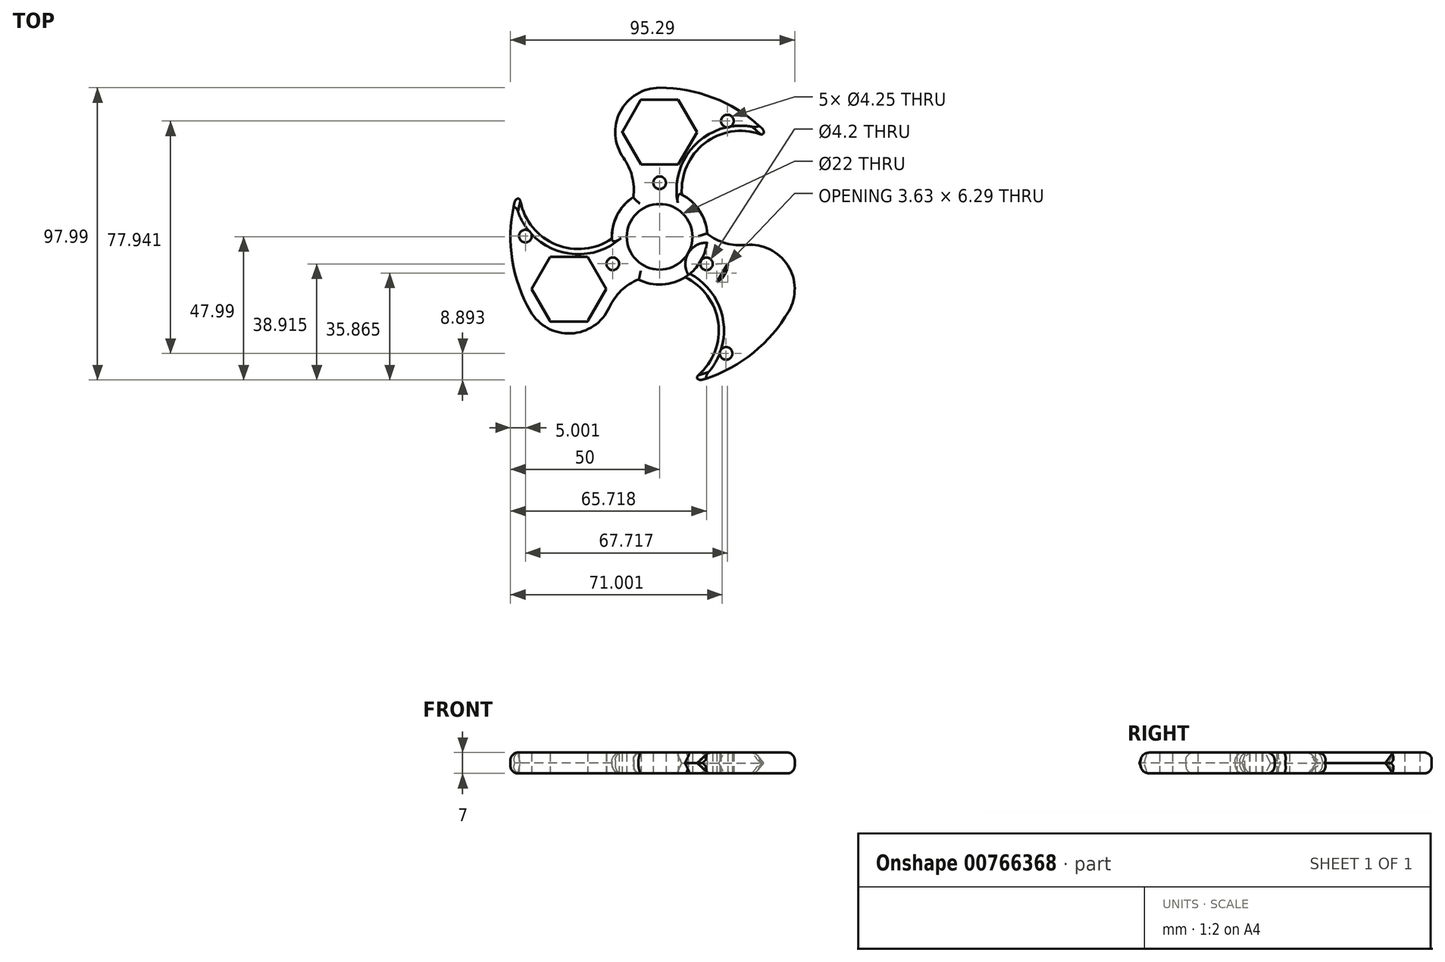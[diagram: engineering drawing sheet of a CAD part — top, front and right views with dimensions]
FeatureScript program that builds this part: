
annotation { "Feature Type Name" : "Feature", "Feature Type Description" : "" }
export const myFeature = defineFeature(function(context is Context, id is Id, definition is map)
    precondition{}
    {
        {
            var Q0;
            Q0=qCreatedBy(makeId("Top.planeOp"),FACE);
            var sketch = newSketch(context, id + "F0", { "sketchPlane" : qUnion([Q0])});
            skCircle(sketch, "E0", {"center": v(0, 0) * mm, "radius": 11 * mm});
            skArc(sketch, "E1", {"start": v(-43.3, 25) * mm, "mid": v(-50, 0) * mm, "end": v(-43.3, -25) * mm});
            skLineSegment(sketch, "E2", {"start": v(0, 50) * mm, "end": v(0, 0) * mm});
            skLineSegment(sketch, "E3", {"start": v(0, 0) * mm, "end": v(-43.3, -25) * mm});
            skLineSegment(sketch, "E4", {"start": v(-43.3, -25) * mm, "end": v(0, 0) * mm});
            skLineSegment(sketch, "E5", {"start": v(0, 0) * mm, "end": v(43.3, -25) * mm});
            skCircle(sketch, "E6.cCircle", {"center": v(0, 35.12) * mm, "radius": 10.88 * mm, "construction": true});
            skLineSegment(sketch, "E6.0", {"start": v(12.56, 35.12) * mm, "end": v(6.28, 24.25) * mm});
            skLineSegment(sketch, "E6.1", {"start": v(6.28, 24.25) * mm, "end": v(-6.28, 24.25) * mm});
            skLineSegment(sketch, "E6.2", {"start": v(-6.28, 24.25) * mm, "end": v(-12.56, 35.13) * mm});
            skLineSegment(sketch, "E6.3", {"start": v(-12.56, 35.13) * mm, "end": v(-6.28, 46) * mm});
            skLineSegment(sketch, "E6.4", {"start": v(-6.28, 46) * mm, "end": v(6.28, 46) * mm});
            skLineSegment(sketch, "E6.5", {"start": v(6.28, 46) * mm, "end": v(12.56, 35.12) * mm});
            skPoint(sketch, "E6.0.midPoint", {"position": v(9.42, 29.69) * mm});
            skCircle(sketch, "E7.cCircle", {"center": v(30.42, -17.56) * mm, "radius": 10.88 * mm, "construction": true});
            skLineSegment(sketch, "E7.0", {"start": v(36.7, -6.69) * mm, "end": v(42.98, -17.56) * mm});
            skLineSegment(sketch, "E7.1", {"start": v(42.98, -17.56) * mm, "end": v(36.7, -28.44) * mm});
            skLineSegment(sketch, "E7.2", {"start": v(36.7, -28.44) * mm, "end": v(24.14, -28.44) * mm});
            skLineSegment(sketch, "E7.3", {"start": v(24.14, -28.44) * mm, "end": v(17.86, -17.56) * mm});
            skLineSegment(sketch, "E7.4", {"start": v(17.86, -17.56) * mm, "end": v(24.14, -6.69) * mm});
            skLineSegment(sketch, "E7.5", {"start": v(24.14, -6.69) * mm, "end": v(36.7, -6.69) * mm});
            skPoint(sketch, "E7.0.midPoint", {"position": v(39.84, -12.12) * mm});
            skCircle(sketch, "E8.cCircle", {"center": v(-30.42, -17.56) * mm, "radius": 10.88 * mm, "construction": true});
            skLineSegment(sketch, "E8.0", {"start": v(-17.86, -17.56) * mm, "end": v(-24.14, -28.44) * mm});
            skLineSegment(sketch, "E8.1", {"start": v(-24.14, -28.44) * mm, "end": v(-36.7, -28.44) * mm});
            skLineSegment(sketch, "E8.2", {"start": v(-36.7, -28.44) * mm, "end": v(-42.98, -17.56) * mm});
            skLineSegment(sketch, "E8.3", {"start": v(-42.98, -17.56) * mm, "end": v(-36.7, -6.69) * mm});
            skLineSegment(sketch, "E8.4", {"start": v(-36.7, -6.69) * mm, "end": v(-24.14, -6.69) * mm});
            skLineSegment(sketch, "E8.5", {"start": v(-24.14, -6.69) * mm, "end": v(-17.86, -17.56) * mm});
            skPoint(sketch, "E8.0.midPoint", {"position": v(-21, -23) * mm});
            skCircle(sketch, "E9", {"center": v(0, 35.12) * mm, "radius": 14.88 * mm});
            skCircle(sketch, "E10", {"center": v(30.42, -17.56) * mm, "radius": 14.88 * mm});
            skCircle(sketch, "E11", {"center": v(-30.42, -17.56) * mm, "radius": 14.87 * mm});
            skCircle(sketch, "E12", {"center": v(0, 0) * mm, "radius": 16 * mm});
            skCircle(sketch, "E13", {"center": v(0, 18.13) * mm, "radius": 2.13 * mm});
            skCircle(sketch, "E14", {"center": v(0, 18.13) * mm, "radius": 7.13 * mm});
            skCircle(sketch, "E15", {"center": v(15.72, -9.07) * mm, "radius": 2.1 * mm});
            skCircle(sketch, "E16", {"center": v(15.72, -9.07) * mm, "radius": 7.1 * mm});
            skCircle(sketch, "E17", {"center": v(-15.7, -9.06) * mm, "radius": 2.13 * mm});
            skCircle(sketch, "E18", {"center": v(-15.7, -9.06) * mm, "radius": 7.13 * mm});
            skLineSegment(sketch, "E19", {"start": v(0, 0) * mm, "end": v(-13.86, 8) * mm});
            skLineSegment(sketch, "E20", {"start": v(0, 0) * mm, "end": v(13.86, 8) * mm});
            skLineSegment(sketch, "E21", {"start": v(0, 0) * mm, "end": v(0, -16) * mm});
            skArc(sketch, "E22", {"start": v(-43.3, 25) * mm, "mid": v(-26.34, -2.82) * mm, "end": v(-12.11, 26.5) * mm});
            skArc(sketch, "E23", {"start": v(43.3, 25) * mm, "mid": v(10.73, 24.22) * mm, "end": v(29, -2.76) * mm});
            skArc(sketch, "E24", {"start": v(0, -50) * mm, "mid": v(15.61, -21.4) * mm, "end": v(-16.89, -23.74) * mm});
            skArc(sketch, "E25.trimOffspring", {"start": v(0, -50) * mm, "mid": v(25, -43.3) * mm, "end": v(43.3, -25) * mm});
            skArc(sketch, "E26.trimOffspring", {"start": v(43.3, 25) * mm, "mid": v(25, 43.3) * mm, "end": v(0, 50) * mm});
            skPoint(sketch, "E27", {"position": v(22.72, 38.84) * mm});
            skPoint(sketch, "E28", {"position": v(22.28, -39.1) * mm});
            skPoint(sketch, "E29", {"position": v(-45, 0.25) * mm});
            skSolve(sketch);
        }
        {
            var Q0;
            {var subQ1=sQuery(id+"F0.wireOp",EDGE,"E6.2");Q0=makeQuery(id+"F0.imprint","IMPRINT",FACE,{"disambiguationData":[TD([[makeQuery(id+"F0.imprint","IMPRINT",EDGE,{"derivedFrom":subQ1}),1.0]])]});}
            var Q1;
            {var subQ5=sQuery(id+"F0.wireOp",EDGE,"E6.0");Q1=makeQuery(id+"F0.imprint","IMPRINT",FACE,{"disambiguationData":[TD([[makeQuery(id+"F0.imprint","IMPRINT",EDGE,{"derivedFrom":subQ5}),1.0]])]});}
            var Q2;
            {var subQ0=sQuery(id+"F0.wireOp",EDGE,"E6.1");var subQ1=sQuery(id+"F0.wireOp",EDGE,"E2");var subQ2=makeQuery(id+"F0.imprint","INTERSECT",VERTEX,{"derivedFrom":[subQ1,subQ0]});Q2=makeQuery(id+"F0.imprint","IMPRINT",FACE,{"disambiguationData":[TD([[makeQuery(id+"F0.imprint","IMPRINT",EDGE,{"disambiguationData":[TD([[subQ2,1.0]])],"derivedFrom":subQ0}),1.0]])]});}
            var Q3;
            {var subQ0=sQuery(id+"F0.wireOp",EDGE,"E6.1");var subQ1=sQuery(id+"F0.wireOp",EDGE,"E2");var subQ2=makeQuery(id+"F0.imprint","INTERSECT",VERTEX,{"derivedFrom":[subQ1,subQ0]});Q3=makeQuery(id+"F0.imprint","IMPRINT",FACE,{"disambiguationData":[TD([[makeQuery(id+"F0.imprint","IMPRINT",EDGE,{"disambiguationData":[TD([[subQ2,-1.0]])],"derivedFrom":subQ0}),1.0]])]});}
            var Q4;
            {var subQ0=sQuery(id+"F0.wireOp",EDGE,"E22");var subQ1=sQuery(id+"F0.wireOp",EDGE,"E9");var subQ2=makeQuery(id+"F0.imprint","INTERSECT",VERTEX,{"derivedFrom":[subQ1,subQ0]});Q4=makeQuery(id+"F0.imprint","IMPRINT",FACE,{"disambiguationData":[TD([[makeQuery(id+"F0.imprint","IMPRINT",EDGE,{"disambiguationData":[TD([[subQ2,-1.0]])],"derivedFrom":subQ1}),-1.0]])]});}
            var Q5;
            {var subQ0=sQuery(id+"F0.wireOp",EDGE,"E23");var subQ1=sQuery(id+"F0.wireOp",EDGE,"E9");var subQ2=makeQuery(id+"F0.imprint","INTERSECT",VERTEX,{"derivedFrom":[subQ1,subQ0]});Q5=makeQuery(id+"F0.imprint","IMPRINT",FACE,{"disambiguationData":[TD([[makeQuery(id+"F0.imprint","IMPRINT",EDGE,{"disambiguationData":[TD([[subQ2,1.0]])],"derivedFrom":subQ1}),-1.0]])]});}
            var Q6;
            {var subQ3=sQuery(id+"F0.wireOp",EDGE,"E22");var subQ5=sQuery(id+"F0.wireOp",EDGE,"E12");var subQ6=makeQuery(id+"F0.imprint","INTERSECT",VERTEX,{"disambiguationData":[OD(0.0)],"derivedFrom":[subQ5,subQ3]});Q6=makeQuery(id+"F0.imprint","IMPRINT",FACE,{"disambiguationData":[TD([[makeQuery(id+"F0.imprint","IMPRINT",EDGE,{"disambiguationData":[TD([[subQ6,1.0]])],"derivedFrom":subQ5}),1.0]])]});}
            var Q7;
            {var subQ1=sQuery(id+"F0.wireOp",EDGE,"E12");var subQ7=sQuery(id+"F0.wireOp",EDGE,"E23");var subQ9=makeQuery(id+"F0.imprint","INTERSECT",VERTEX,{"disambiguationData":[OD(1.0)],"derivedFrom":[subQ1,subQ7]});Q7=makeQuery(id+"F0.imprint","IMPRINT",FACE,{"disambiguationData":[TD([[makeQuery(id+"F0.imprint","IMPRINT",EDGE,{"disambiguationData":[TD([[subQ9,-1.0]])],"derivedFrom":subQ1}),1.0]])]});}
            var Q8;
            {var subQ1=sQuery(id+"F0.wireOp",EDGE,"E12");var subQ5=sQuery(id+"F0.wireOp",EDGE,"E22");var subQ6=makeQuery(id+"F0.imprint","INTERSECT",VERTEX,{"disambiguationData":[OD(1.0)],"derivedFrom":[subQ1,subQ5]});Q8=makeQuery(id+"F0.imprint","IMPRINT",FACE,{"disambiguationData":[TD([[makeQuery(id+"F0.imprint","IMPRINT",EDGE,{"disambiguationData":[TD([[subQ6,-1.0]])],"derivedFrom":subQ1}),1.0]])]});}
            var Q9;
            {var subQ1=sQuery(id+"F0.wireOp",EDGE,"E12");var subQ5=sQuery(id+"F0.wireOp",EDGE,"E24");var subQ6=makeQuery(id+"F0.imprint","INTERSECT",VERTEX,{"disambiguationData":[OD(0.0)],"derivedFrom":[subQ1,subQ5]});Q9=makeQuery(id+"F0.imprint","IMPRINT",FACE,{"disambiguationData":[TD([[makeQuery(id+"F0.imprint","IMPRINT",EDGE,{"disambiguationData":[TD([[subQ6,1.0]])],"derivedFrom":subQ1}),1.0]])]});}
            var Q10;
            {var subQ5=sQuery(id+"F0.wireOp",EDGE,"E21");var subQ6=sQuery(id+"F0.wireOp",EDGE,"E0");var subQ7=makeQuery(id+"F0.imprint","INTERSECT",VERTEX,{"derivedFrom":[subQ6,subQ5]});Q10=makeQuery(id+"F0.imprint","IMPRINT",FACE,{"disambiguationData":[TD([[makeQuery(id+"F0.imprint","IMPRINT",EDGE,{"disambiguationData":[TD([[subQ7,-1.0]])],"derivedFrom":subQ6}),-1.0]])]});}
            var Q11;
            {var subQ1=sQuery(id+"F0.wireOp",EDGE,"E0");var subQ9=sQuery(id+"F0.wireOp",EDGE,"E20");var subQ11=makeQuery(id+"F0.imprint","INTERSECT",VERTEX,{"derivedFrom":[subQ1,subQ9]});Q11=makeQuery(id+"F0.imprint","IMPRINT",FACE,{"disambiguationData":[TD([[makeQuery(id+"F0.imprint","IMPRINT",EDGE,{"disambiguationData":[TD([[subQ11,1.0]])],"derivedFrom":subQ1}),-1.0]])]});}
            var Q12;
            {var subQ0=sQuery(id+"F0.wireOp",EDGE,"E23");var subQ1=sQuery(id+"F0.wireOp",EDGE,"E10");var subQ2=makeQuery(id+"F0.imprint","INTERSECT",VERTEX,{"derivedFrom":[subQ1,subQ0]});Q12=makeQuery(id+"F0.imprint","IMPRINT",FACE,{"disambiguationData":[TD([[makeQuery(id+"F0.imprint","IMPRINT",EDGE,{"disambiguationData":[TD([[subQ2,-1.0]])],"derivedFrom":subQ1}),-1.0]])]});}
            var Q13;
            {var subQ0=sQuery(id+"F0.wireOp",EDGE,"E24");var subQ1=sQuery(id+"F0.wireOp",EDGE,"E10");var subQ2=makeQuery(id+"F0.imprint","INTERSECT",VERTEX,{"derivedFrom":[subQ1,subQ0]});Q13=makeQuery(id+"F0.imprint","IMPRINT",FACE,{"disambiguationData":[TD([[makeQuery(id+"F0.imprint","IMPRINT",EDGE,{"disambiguationData":[TD([[subQ2,1.0]])],"derivedFrom":subQ1}),-1.0]])]});}
            var Q14;
            {var subQ0=sQuery(id+"F0.wireOp",EDGE,"E7.2");Q14=makeQuery(id+"F0.imprint","IMPRINT",FACE,{"disambiguationData":[TD([[makeQuery(id+"F0.imprint","IMPRINT",EDGE,{"derivedFrom":subQ0}),1.0]])]});}
            var Q15;
            {var subQ5=sQuery(id+"F0.wireOp",EDGE,"E7.0");Q15=makeQuery(id+"F0.imprint","IMPRINT",FACE,{"disambiguationData":[TD([[makeQuery(id+"F0.imprint","IMPRINT",EDGE,{"derivedFrom":subQ5}),1.0]])]});}
            var Q16;
            {var subQ0=sQuery(id+"F0.wireOp",EDGE,"E25.trimOffspring");Q16=makeQuery(id+"F0.imprint","IMPRINT",FACE,{"disambiguationData":[TD([[makeQuery(id+"F0.imprint","IMPRINT",EDGE,{"derivedFrom":subQ0}),1.0]])]});}
            var Q17;
            {var subQ0=sQuery(id+"F0.wireOp",EDGE,"E7.4");var subQ1=sQuery(id+"F0.wireOp",EDGE,"E5");var subQ2=makeQuery(id+"F0.imprint","INTERSECT",VERTEX,{"derivedFrom":[subQ1,subQ0]});Q17=makeQuery(id+"F0.imprint","IMPRINT",FACE,{"disambiguationData":[TD([[makeQuery(id+"F0.imprint","IMPRINT",EDGE,{"disambiguationData":[TD([[subQ2,1.0]])],"derivedFrom":subQ0}),1.0]])]});}
            var Q18;
            {var subQ0=sQuery(id+"F0.wireOp",EDGE,"E7.4");var subQ1=sQuery(id+"F0.wireOp",EDGE,"E5");var subQ2=makeQuery(id+"F0.imprint","INTERSECT",VERTEX,{"derivedFrom":[subQ1,subQ0]});Q18=makeQuery(id+"F0.imprint","IMPRINT",FACE,{"disambiguationData":[TD([[makeQuery(id+"F0.imprint","IMPRINT",EDGE,{"disambiguationData":[TD([[subQ2,-1.0]])],"derivedFrom":subQ0}),1.0]])]});}
            var Q19;
            {var subQ0=sQuery(id+"F0.wireOp",EDGE,"E26.trimOffspring");Q19=makeQuery(id+"F0.imprint","IMPRINT",FACE,{"disambiguationData":[TD([[makeQuery(id+"F0.imprint","IMPRINT",EDGE,{"derivedFrom":subQ0}),1.0]])]});}
            var Q20;
            {var subQ0=sQuery(id+"F0.wireOp",EDGE,"E14");var subQ1=sQuery(id+"F0.wireOp",EDGE,"E9");var subQ2=makeQuery(id+"F0.imprint","INTERSECT",VERTEX,{"disambiguationData":[OD(0.0)],"derivedFrom":[subQ1,subQ0]});Q20=makeQuery(id+"F0.imprint","IMPRINT",FACE,{"disambiguationData":[TD([[makeQuery(id+"F0.imprint","IMPRINT",EDGE,{"disambiguationData":[TD([[subQ2,-1.0]])],"derivedFrom":subQ0}),1.0]])]});}
            var Q21;
            {var subQ0=sQuery(id+"F0.wireOp",EDGE,"E14");var subQ1=sQuery(id+"F0.wireOp",EDGE,"E9");var subQ2=makeQuery(id+"F0.imprint","INTERSECT",VERTEX,{"disambiguationData":[OD(1.0)],"derivedFrom":[subQ1,subQ0]});Q21=makeQuery(id+"F0.imprint","IMPRINT",FACE,{"disambiguationData":[TD([[makeQuery(id+"F0.imprint","IMPRINT",EDGE,{"disambiguationData":[TD([[subQ2,1.0]])],"derivedFrom":subQ0}),1.0]])]});}
            var Q22;
            {var subQ0=sQuery(id+"F0.wireOp",EDGE,"E14");var subQ3=sQuery(id+"F0.wireOp",EDGE,"E12");var subQ5=makeQuery(id+"F0.imprint","INTERSECT",VERTEX,{"disambiguationData":[OD(0.0)],"derivedFrom":[subQ3,subQ0]});Q22=makeQuery(id+"F0.imprint","IMPRINT",FACE,{"disambiguationData":[TD([[makeQuery(id+"F0.imprint","IMPRINT",EDGE,{"disambiguationData":[TD([[subQ5,-1.0]])],"derivedFrom":subQ3}),1.0]])]});}
            var Q23;
            {var subQ0=sQuery(id+"F0.wireOp",EDGE,"E14");var subQ3=sQuery(id+"F0.wireOp",EDGE,"E12");var subQ5=makeQuery(id+"F0.imprint","INTERSECT",VERTEX,{"disambiguationData":[OD(1.0)],"derivedFrom":[subQ3,subQ0]});Q23=makeQuery(id+"F0.imprint","IMPRINT",FACE,{"disambiguationData":[TD([[makeQuery(id+"F0.imprint","IMPRINT",EDGE,{"disambiguationData":[TD([[subQ5,1.0]])],"derivedFrom":subQ3}),1.0]])]});}
            var Q24;
            {var subQ0=sQuery(id+"F0.wireOp",EDGE,"E16");var subQ1=sQuery(id+"F0.wireOp",EDGE,"E5");var subQ2=makeQuery(id+"F0.imprint","INTERSECT",VERTEX,{"disambiguationData":[OD(0.0)],"derivedFrom":[subQ1,subQ0]});Q24=makeQuery(id+"F0.imprint","IMPRINT",FACE,{"disambiguationData":[TD([[makeQuery(id+"F0.imprint","IMPRINT",EDGE,{"disambiguationData":[TD([[subQ2,-1.0]])],"derivedFrom":subQ1}),1.0]])]});}
            var Q25;
            {var subQ0=sQuery(id+"F0.wireOp",EDGE,"E16");var subQ1=sQuery(id+"F0.wireOp",EDGE,"E5");var subQ2=makeQuery(id+"F0.imprint","INTERSECT",VERTEX,{"disambiguationData":[OD(0.0)],"derivedFrom":[subQ1,subQ0]});Q25=makeQuery(id+"F0.imprint","IMPRINT",FACE,{"disambiguationData":[TD([[makeQuery(id+"F0.imprint","IMPRINT",EDGE,{"disambiguationData":[TD([[subQ2,-1.0]])],"derivedFrom":subQ1}),-1.0]])]});}
            var Q26;
            {var subQ1=sQuery(id+"F0.wireOp",EDGE,"E5");var subQ5=sQuery(id+"F0.wireOp",EDGE,"E12");var subQ6=makeQuery(id+"F0.imprint","INTERSECT",VERTEX,{"derivedFrom":[subQ1,subQ5]});Q26=makeQuery(id+"F0.imprint","IMPRINT",FACE,{"disambiguationData":[TD([[makeQuery(id+"F0.imprint","IMPRINT",EDGE,{"disambiguationData":[TD([[subQ6,-1.0]])],"derivedFrom":subQ1}),-1.0]])]});}
            var Q27;
            {var subQ1=sQuery(id+"F0.wireOp",EDGE,"E5");var subQ7=sQuery(id+"F0.wireOp",EDGE,"E12");var subQ8=makeQuery(id+"F0.imprint","INTERSECT",VERTEX,{"derivedFrom":[subQ1,subQ7]});Q27=makeQuery(id+"F0.imprint","IMPRINT",FACE,{"disambiguationData":[TD([[makeQuery(id+"F0.imprint","IMPRINT",EDGE,{"disambiguationData":[TD([[subQ8,-1.0]])],"derivedFrom":subQ1}),1.0]])]});}
            var Q28;
            {var subQ0=sQuery(id+"F0.wireOp",EDGE,"E1");Q28=makeQuery(id+"F0.imprint","IMPRINT",FACE,{"disambiguationData":[TD([[makeQuery(id+"F0.imprint","IMPRINT",EDGE,{"derivedFrom":subQ0}),1.0]])]});}
            var Q29;
            {var subQ1=sQuery(id+"F0.wireOp",EDGE,"E8.3");Q29=makeQuery(id+"F0.imprint","IMPRINT",FACE,{"disambiguationData":[TD([[makeQuery(id+"F0.imprint","IMPRINT",EDGE,{"derivedFrom":subQ1}),1.0]])]});}
            var Q30;
            {var subQ4=sQuery(id+"F0.wireOp",EDGE,"E8.0");Q30=makeQuery(id+"F0.imprint","IMPRINT",FACE,{"disambiguationData":[TD([[makeQuery(id+"F0.imprint","IMPRINT",EDGE,{"derivedFrom":subQ4}),1.0]])]});}
            var Q31;
            {var subQ0=sQuery(id+"F0.wireOp",EDGE,"E24");var subQ1=sQuery(id+"F0.wireOp",EDGE,"E11");var subQ2=makeQuery(id+"F0.imprint","INTERSECT",VERTEX,{"derivedFrom":[subQ1,subQ0]});Q31=makeQuery(id+"F0.imprint","IMPRINT",FACE,{"disambiguationData":[TD([[makeQuery(id+"F0.imprint","IMPRINT",EDGE,{"disambiguationData":[TD([[subQ2,-1.0]])],"derivedFrom":subQ1}),-1.0]])]});}
            var Q32;
            {var subQ0=sQuery(id+"F0.wireOp",EDGE,"E22");var subQ1=sQuery(id+"F0.wireOp",EDGE,"E11");var subQ2=makeQuery(id+"F0.imprint","INTERSECT",VERTEX,{"derivedFrom":[subQ1,subQ0]});Q32=makeQuery(id+"F0.imprint","IMPRINT",FACE,{"disambiguationData":[TD([[makeQuery(id+"F0.imprint","IMPRINT",EDGE,{"disambiguationData":[TD([[subQ2,1.0]])],"derivedFrom":subQ1}),-1.0]])]});}
            var Q33;
            {var subQ0=sQuery(id+"F0.wireOp",EDGE,"E8.5");var subQ1=sQuery(id+"F0.wireOp",EDGE,"E4");var subQ2=makeQuery(id+"F0.imprint","INTERSECT",VERTEX,{"derivedFrom":[subQ1,subQ0]});Q33=makeQuery(id+"F0.imprint","IMPRINT",FACE,{"disambiguationData":[TD([[makeQuery(id+"F0.imprint","IMPRINT",EDGE,{"disambiguationData":[TD([[subQ2,-1.0]])],"derivedFrom":subQ0}),1.0]])]});}
            var Q34;
            {var subQ0=sQuery(id+"F0.wireOp",EDGE,"E8.5");var subQ1=sQuery(id+"F0.wireOp",EDGE,"E4");var subQ2=makeQuery(id+"F0.imprint","INTERSECT",VERTEX,{"derivedFrom":[subQ1,subQ0]});Q34=makeQuery(id+"F0.imprint","IMPRINT",FACE,{"disambiguationData":[TD([[makeQuery(id+"F0.imprint","IMPRINT",EDGE,{"disambiguationData":[TD([[subQ2,1.0]])],"derivedFrom":subQ0}),1.0]])]});}
            var Q35;
            {var subQ0=sQuery(id+"F0.wireOp",EDGE,"E18");var subQ1=sQuery(id+"F0.wireOp",EDGE,"E11");var subQ2=makeQuery(id+"F0.imprint","INTERSECT",VERTEX,{"disambiguationData":[OD(1.0)],"derivedFrom":[subQ1,subQ0]});Q35=makeQuery(id+"F0.imprint","IMPRINT",FACE,{"disambiguationData":[TD([[makeQuery(id+"F0.imprint","IMPRINT",EDGE,{"disambiguationData":[TD([[subQ2,1.0]])],"derivedFrom":subQ0}),1.0]])]});}
            var Q36;
            {var subQ0=sQuery(id+"F0.wireOp",EDGE,"E18");var subQ1=sQuery(id+"F0.wireOp",EDGE,"E11");var subQ2=makeQuery(id+"F0.imprint","INTERSECT",VERTEX,{"disambiguationData":[OD(0.0)],"derivedFrom":[subQ1,subQ0]});Q36=makeQuery(id+"F0.imprint","IMPRINT",FACE,{"disambiguationData":[TD([[makeQuery(id+"F0.imprint","IMPRINT",EDGE,{"disambiguationData":[TD([[subQ2,-1.0]])],"derivedFrom":subQ0}),1.0]])]});}
            var Q37;
            {var subQ0=sQuery(id+"F0.wireOp",EDGE,"E18");var subQ3=sQuery(id+"F0.wireOp",EDGE,"E12");var subQ5=makeQuery(id+"F0.imprint","INTERSECT",VERTEX,{"disambiguationData":[OD(1.0)],"derivedFrom":[subQ3,subQ0]});Q37=makeQuery(id+"F0.imprint","IMPRINT",FACE,{"disambiguationData":[TD([[makeQuery(id+"F0.imprint","IMPRINT",EDGE,{"disambiguationData":[TD([[subQ5,1.0]])],"derivedFrom":subQ3}),1.0]])]});}
            var Q38;
            {var subQ0=sQuery(id+"F0.wireOp",EDGE,"E18");var subQ3=sQuery(id+"F0.wireOp",EDGE,"E12");var subQ5=makeQuery(id+"F0.imprint","INTERSECT",VERTEX,{"disambiguationData":[OD(0.0)],"derivedFrom":[subQ3,subQ0]});Q38=makeQuery(id+"F0.imprint","IMPRINT",FACE,{"disambiguationData":[TD([[makeQuery(id+"F0.imprint","IMPRINT",EDGE,{"disambiguationData":[TD([[subQ5,-1.0]])],"derivedFrom":subQ3}),1.0]])]});}
            var Q39;
            {var subQ0=sQuery(id+"F0.wireOp",EDGE,"E19");var subQ1=sQuery(id+"F0.wireOp",EDGE,"E12");var subQ2=makeQuery(id+"F0.imprint","INTERSECT",VERTEX,{"derivedFrom":[subQ1,subQ0]});Q39=makeQuery(id+"F0.imprint","IMPRINT",FACE,{"disambiguationData":[TD([[makeQuery(id+"F0.imprint","IMPRINT",EDGE,{"disambiguationData":[TD([[subQ2,-1.0]])],"derivedFrom":subQ1}),1.0]])]});}
            var Q40;
            {var subQ0=sQuery(id+"F0.wireOp",EDGE,"E19");var subQ1=sQuery(id+"F0.wireOp",EDGE,"E12");var subQ2=makeQuery(id+"F0.imprint","INTERSECT",VERTEX,{"derivedFrom":[subQ1,subQ0]});Q40=makeQuery(id+"F0.imprint","IMPRINT",FACE,{"disambiguationData":[TD([[makeQuery(id+"F0.imprint","IMPRINT",EDGE,{"disambiguationData":[TD([[subQ2,1.0]])],"derivedFrom":subQ1}),1.0]])]});}
            var Q41;
            {var subQ0=sQuery(id+"F0.wireOp",EDGE,"E20");var subQ1=sQuery(id+"F0.wireOp",EDGE,"E12");var subQ2=makeQuery(id+"F0.imprint","INTERSECT",VERTEX,{"derivedFrom":[subQ1,subQ0]});Q41=makeQuery(id+"F0.imprint","IMPRINT",FACE,{"disambiguationData":[TD([[makeQuery(id+"F0.imprint","IMPRINT",EDGE,{"disambiguationData":[TD([[subQ2,-1.0]])],"derivedFrom":subQ1}),1.0]])]});}
            var Q42;
            {var subQ0=sQuery(id+"F0.wireOp",EDGE,"E20");var subQ1=sQuery(id+"F0.wireOp",EDGE,"E12");var subQ2=makeQuery(id+"F0.imprint","INTERSECT",VERTEX,{"derivedFrom":[subQ1,subQ0]});Q42=makeQuery(id+"F0.imprint","IMPRINT",FACE,{"disambiguationData":[TD([[makeQuery(id+"F0.imprint","IMPRINT",EDGE,{"disambiguationData":[TD([[subQ2,1.0]])],"derivedFrom":subQ1}),1.0]])]});}
            var Q43;
            {var subQ0=sQuery(id+"F0.wireOp",EDGE,"E21");var subQ1=sQuery(id+"F0.wireOp",EDGE,"E12");var subQ2=makeQuery(id+"F0.imprint","INTERSECT",VERTEX,{"derivedFrom":[subQ1,subQ0]});Q43=makeQuery(id+"F0.imprint","IMPRINT",FACE,{"disambiguationData":[TD([[makeQuery(id+"F0.imprint","IMPRINT",EDGE,{"disambiguationData":[TD([[subQ2,-1.0]])],"derivedFrom":subQ1}),1.0]])]});}
            var Q44;
            {var subQ0=sQuery(id+"F0.wireOp",EDGE,"E21");var subQ1=sQuery(id+"F0.wireOp",EDGE,"E12");var subQ2=makeQuery(id+"F0.imprint","INTERSECT",VERTEX,{"derivedFrom":[subQ1,subQ0]});Q44=makeQuery(id+"F0.imprint","IMPRINT",FACE,{"disambiguationData":[TD([[makeQuery(id+"F0.imprint","IMPRINT",EDGE,{"disambiguationData":[TD([[subQ2,1.0]])],"derivedFrom":subQ1}),1.0]])]});}
            extrude(context, id + "F1", {"entities" : qUnion([Q0, Q1, Q2, Q3, Q4, Q5, Q6, Q7, Q8, Q9, Q10, Q11, Q12, Q13, Q14, Q15, Q16, Q17, Q18, Q19, Q20, Q21, Q22, Q23, Q24, Q25, Q26, Q27, Q28, Q29, Q30, Q31, Q32, Q33, Q34, Q35, Q36, Q37, Q38, Q39, Q40, Q41, Q42, Q43, Q44]), "depth" : 7 * mm, "offsetDistance" : 25 * mm});
        }
        {
            var Q0;
            Q0=sQuery(id+"F0.wireOp",VERTEX,"E27");
            var Q1;
            Q1=sQuery(id+"F0.wireOp",VERTEX,"E28");
            var Q2;
            Q2=sQuery(id+"F0.wireOp",VERTEX,"E29");
            var Q3;
            Q3=makeQuery(id+"F1.opExtrude","SWEPT_BODY",BODY,{"disambiguationData":[OSD([sQuery(id+"F0.wireOp",EDGE,"E0"),sQuery(id+"F0.wireOp",EDGE,"E1"),sQuery(id+"F0.wireOp",EDGE,"E6.0"),sQuery(id+"F0.wireOp",EDGE,"E6.1"),sQuery(id+"F0.wireOp",EDGE,"E6.2"),sQuery(id+"F0.wireOp",EDGE,"E6.3"),sQuery(id+"F0.wireOp",EDGE,"E6.4"),sQuery(id+"F0.wireOp",EDGE,"E6.5"),sQuery(id+"F0.wireOp",EDGE,"E7.0"),sQuery(id+"F0.wireOp",EDGE,"E7.1"),sQuery(id+"F0.wireOp",EDGE,"E7.2"),sQuery(id+"F0.wireOp",EDGE,"E7.3"),sQuery(id+"F0.wireOp",EDGE,"E7.4"),sQuery(id+"F0.wireOp",EDGE,"E7.5"),sQuery(id+"F0.wireOp",EDGE,"E8.0"),sQuery(id+"F0.wireOp",EDGE,"E8.1"),sQuery(id+"F0.wireOp",EDGE,"E8.2"),sQuery(id+"F0.wireOp",EDGE,"E8.3"),sQuery(id+"F0.wireOp",EDGE,"E8.4"),sQuery(id+"F0.wireOp",EDGE,"E8.5"),sQuery(id+"F0.wireOp",EDGE,"E9"),sQuery(id+"F0.wireOp",EDGE,"E10"),sQuery(id+"F0.wireOp",EDGE,"E11"),sQuery(id+"F0.wireOp",EDGE,"E13"),sQuery(id+"F0.wireOp",EDGE,"E15"),sQuery(id+"F0.wireOp",EDGE,"E17"),sQuery(id+"F0.wireOp",EDGE,"E22"),sQuery(id+"F0.wireOp",EDGE,"E23"),sQuery(id+"F0.wireOp",EDGE,"E24"),sQuery(id+"F0.wireOp",EDGE,"E25.trimOffspring"),sQuery(id+"F0.wireOp",EDGE,"E26.trimOffspring")])]});
            hole(context, id + "F2", {"style" : HoleStyle.SIMPLE, "endStyle" : HoleEndStyle.THROUGH, "oppositeDirection" : true, "holeDiameter" : 4.25 * mm, "majorDiameter" : 5 * mm, "isTappedThrough" : true, "tappedDepth" : 12 * mm, "tapClearance" : 3, "startFromSketch" : true, "locations" : qUnion([Q0, Q1, Q2]), "scope" : qUnion([Q3])});
        }
        {
            var Q0;
            {var subQ0=sQuery(id+"F0.wireOp",EDGE,"E22");var subQ1=makeQuery(id+"F0.imprint","INTERSECT",VERTEX,{"derivedFrom":[sQuery(id+"F0.wireOp",EDGE,"E11"),subQ0]});Q0=makeQuery(id+"F1.opExtrude","CAP_EDGE",EDGE,{"disambiguationData":[OSD([subQ0]),TDD([makeQuery(id+"F0.imprint","IMPRINT",EDGE,{"disambiguationData":[TD([[makeQuery(id+"F0.imprint","INTERSECT",VERTEX,{"derivedFrom":[sQuery(id+"F0.wireOp",EDGE,"E1"),subQ0]}),-1.0]])],"derivedFrom":subQ0}),makeQuery(id+"F0.imprint","IMPRINT",EDGE,{"disambiguationData":[TD([[subQ1,-1.0]])],"derivedFrom":subQ0})])],"isStart":false});}
            var Q1;
            {var subQ0=sQuery(id+"F0.wireOp",EDGE,"E23");var subQ1=makeQuery(id+"F0.imprint","INTERSECT",VERTEX,{"derivedFrom":[sQuery(id+"F0.wireOp",EDGE,"E9"),subQ0]});Q1=makeQuery(id+"F1.opExtrude","CAP_EDGE",EDGE,{"disambiguationData":[OSD([subQ0]),TDD([makeQuery(id+"F0.imprint","IMPRINT",EDGE,{"disambiguationData":[TD([[makeQuery(id+"F0.imprint","INTERSECT",VERTEX,{"derivedFrom":[subQ0,sQuery(id+"F0.wireOp",EDGE,"E26.trimOffspring")]}),-1.0]])],"derivedFrom":subQ0}),makeQuery(id+"F0.imprint","IMPRINT",EDGE,{"disambiguationData":[TD([[subQ1,-1.0]])],"derivedFrom":subQ0})])],"isStart":false});}
            var Q2;
            {var subQ0=sQuery(id+"F0.wireOp",EDGE,"E24");var subQ1=makeQuery(id+"F0.imprint","INTERSECT",VERTEX,{"derivedFrom":[sQuery(id+"F0.wireOp",EDGE,"E10"),subQ0]});Q2=makeQuery(id+"F1.opExtrude","CAP_EDGE",EDGE,{"disambiguationData":[OSD([subQ0]),TDD([makeQuery(id+"F0.imprint","IMPRINT",EDGE,{"disambiguationData":[TD([[makeQuery(id+"F0.imprint","INTERSECT",VERTEX,{"derivedFrom":[subQ0,sQuery(id+"F0.wireOp",EDGE,"E25.trimOffspring")]}),-1.0]])],"derivedFrom":subQ0}),makeQuery(id+"F0.imprint","IMPRINT",EDGE,{"disambiguationData":[TD([[subQ1,-1.0]])],"derivedFrom":subQ0})])],"isStart":false});}
            chamfer(context, id + "F3", {"entities" : qUnion([Q0, Q1, Q2]), "chamferType" : ChamferType.TWO_OFFSETS, "width1" : 6 * mm, "oppositeDirection" : false, "width2" : 3 * mm, "tangentPropagation" : true});
        }
        {
            var Q0;
            {var subQ0=sQuery(id+"F0.wireOp",EDGE,"E24");var subQ1=makeQuery(id+"F0.imprint","INTERSECT",VERTEX,{"derivedFrom":[sQuery(id+"F0.wireOp",EDGE,"E10"),subQ0]});Q0=makeQuery(id+"F1.opExtrude","CAP_EDGE",EDGE,{"disambiguationData":[OSD([subQ0]),TDD([makeQuery(id+"F0.imprint","IMPRINT",EDGE,{"disambiguationData":[TD([[makeQuery(id+"F0.imprint","INTERSECT",VERTEX,{"derivedFrom":[subQ0,sQuery(id+"F0.wireOp",EDGE,"E25.trimOffspring")]}),-1.0]])],"derivedFrom":subQ0}),makeQuery(id+"F0.imprint","IMPRINT",EDGE,{"disambiguationData":[TD([[subQ1,-1.0]])],"derivedFrom":subQ0})])],"isStart":true});}
            var Q1;
            {var subQ0=sQuery(id+"F0.wireOp",EDGE,"E23");var subQ1=makeQuery(id+"F0.imprint","INTERSECT",VERTEX,{"derivedFrom":[sQuery(id+"F0.wireOp",EDGE,"E9"),subQ0]});Q1=makeQuery(id+"F1.opExtrude","CAP_EDGE",EDGE,{"disambiguationData":[OSD([subQ0]),TDD([makeQuery(id+"F0.imprint","IMPRINT",EDGE,{"disambiguationData":[TD([[makeQuery(id+"F0.imprint","INTERSECT",VERTEX,{"derivedFrom":[subQ0,sQuery(id+"F0.wireOp",EDGE,"E26.trimOffspring")]}),-1.0]])],"derivedFrom":subQ0}),makeQuery(id+"F0.imprint","IMPRINT",EDGE,{"disambiguationData":[TD([[subQ1,-1.0]])],"derivedFrom":subQ0})])],"isStart":true});}
            var Q2;
            {var subQ0=sQuery(id+"F0.wireOp",EDGE,"E22");var subQ1=makeQuery(id+"F0.imprint","INTERSECT",VERTEX,{"derivedFrom":[sQuery(id+"F0.wireOp",EDGE,"E11"),subQ0]});Q2=makeQuery(id+"F1.opExtrude","CAP_EDGE",EDGE,{"disambiguationData":[OSD([subQ0]),TDD([makeQuery(id+"F0.imprint","IMPRINT",EDGE,{"disambiguationData":[TD([[makeQuery(id+"F0.imprint","INTERSECT",VERTEX,{"derivedFrom":[sQuery(id+"F0.wireOp",EDGE,"E1"),subQ0]}),-1.0]])],"derivedFrom":subQ0}),makeQuery(id+"F0.imprint","IMPRINT",EDGE,{"disambiguationData":[TD([[subQ1,-1.0]])],"derivedFrom":subQ0})])],"isStart":true});}
            chamfer(context, id + "F4", {"entities" : qUnion([Q0, Q1, Q2]), "chamferType" : ChamferType.TWO_OFFSETS, "width1" : 3 * mm, "oppositeDirection" : false, "width2" : 6 * mm, "tangentPropagation" : true});
        }
        {
            var Q0;
            {var subQ0=sQuery(id+"F0.wireOp",EDGE,"E12");var subQ1=makeQuery(id+"F0.imprint","INTERSECT",VERTEX,{"derivedFrom":[subQ0,sQuery(id+"F0.wireOp",EDGE,"E19")]});Q0=makeQuery(id+"F1.opExtrude","CAP_EDGE",EDGE,{"disambiguationData":[OSD([subQ0]),TDD([makeQuery(id+"F0.imprint","IMPRINT",EDGE,{"disambiguationData":[TD([[subQ1,1.0]])],"derivedFrom":subQ0}),makeQuery(id+"F0.imprint","IMPRINT",EDGE,{"disambiguationData":[TD([[subQ1,-1.0]])],"derivedFrom":subQ0})])],"isStart":true});}
            var Q1;
            {var subQ0=sQuery(id+"F0.wireOp",EDGE,"E12");var subQ1=makeQuery(id+"F0.imprint","INTERSECT",VERTEX,{"derivedFrom":[subQ0,sQuery(id+"F0.wireOp",EDGE,"E21")]});Q1=makeQuery(id+"F1.opExtrude","CAP_EDGE",EDGE,{"disambiguationData":[OSD([subQ0]),TDD([makeQuery(id+"F0.imprint","IMPRINT",EDGE,{"disambiguationData":[TD([[subQ1,1.0]])],"derivedFrom":subQ0}),makeQuery(id+"F0.imprint","IMPRINT",EDGE,{"disambiguationData":[TD([[subQ1,-1.0]])],"derivedFrom":subQ0})])],"isStart":true});}
            var Q2;
            {var subQ0=sQuery(id+"F0.wireOp",EDGE,"E12");var subQ1=makeQuery(id+"F0.imprint","INTERSECT",VERTEX,{"derivedFrom":[subQ0,sQuery(id+"F0.wireOp",EDGE,"E20")]});Q2=makeQuery(id+"F1.opExtrude","CAP_EDGE",EDGE,{"disambiguationData":[OSD([subQ0]),TDD([makeQuery(id+"F0.imprint","IMPRINT",EDGE,{"disambiguationData":[TD([[subQ1,1.0]])],"derivedFrom":subQ0}),makeQuery(id+"F0.imprint","IMPRINT",EDGE,{"disambiguationData":[TD([[subQ1,-1.0]])],"derivedFrom":subQ0})])],"isStart":true});}
            var Q3;
            {var subQ0=sQuery(id+"F0.wireOp",EDGE,"E12");var subQ1=makeQuery(id+"F0.imprint","INTERSECT",VERTEX,{"derivedFrom":[subQ0,sQuery(id+"F0.wireOp",EDGE,"E19")]});Q3=makeQuery(id+"F1.opExtrude","CAP_EDGE",EDGE,{"disambiguationData":[OSD([subQ0]),TDD([makeQuery(id+"F0.imprint","IMPRINT",EDGE,{"disambiguationData":[TD([[subQ1,1.0]])],"derivedFrom":subQ0}),makeQuery(id+"F0.imprint","IMPRINT",EDGE,{"disambiguationData":[TD([[subQ1,-1.0]])],"derivedFrom":subQ0})])],"isStart":false});}
            var Q4;
            {var subQ0=sQuery(id+"F0.wireOp",EDGE,"E12");var subQ1=makeQuery(id+"F0.imprint","INTERSECT",VERTEX,{"derivedFrom":[subQ0,sQuery(id+"F0.wireOp",EDGE,"E21")]});Q4=makeQuery(id+"F1.opExtrude","CAP_EDGE",EDGE,{"disambiguationData":[OSD([subQ0]),TDD([makeQuery(id+"F0.imprint","IMPRINT",EDGE,{"disambiguationData":[TD([[subQ1,1.0]])],"derivedFrom":subQ0}),makeQuery(id+"F0.imprint","IMPRINT",EDGE,{"disambiguationData":[TD([[subQ1,-1.0]])],"derivedFrom":subQ0})])],"isStart":false});}
            var Q5;
            {var subQ0=sQuery(id+"F0.wireOp",EDGE,"E12");var subQ1=makeQuery(id+"F0.imprint","INTERSECT",VERTEX,{"derivedFrom":[subQ0,sQuery(id+"F0.wireOp",EDGE,"E20")]});Q5=makeQuery(id+"F1.opExtrude","CAP_EDGE",EDGE,{"disambiguationData":[OSD([subQ0]),TDD([makeQuery(id+"F0.imprint","IMPRINT",EDGE,{"disambiguationData":[TD([[subQ1,1.0]])],"derivedFrom":subQ0}),makeQuery(id+"F0.imprint","IMPRINT",EDGE,{"disambiguationData":[TD([[subQ1,-1.0]])],"derivedFrom":subQ0})])],"isStart":false});}
            fillet(context, id + "F5", {"entities" : qUnion([Q0, Q1, Q2, Q3, Q4, Q5]), "radius" : 3 * mm, "tangentPropagation" : true, "allowEdgeOverflow" : false});
        }
        {
            var Q0;
            Q0=makeQuery(id+"F1.opExtrude","CAP_EDGE",EDGE,{"disambiguationData":[OSD([sQuery(id+"F0.wireOp",EDGE,"E11")])],"isStart":true});
            var Q1;
            Q1=makeQuery(id+"F1.opExtrude","CAP_EDGE",EDGE,{"disambiguationData":[OSD([sQuery(id+"F0.wireOp",EDGE,"E9")])],"isStart":true});
            var Q2;
            Q2=makeQuery(id+"F1.opExtrude","CAP_EDGE",EDGE,{"disambiguationData":[OSD([sQuery(id+"F0.wireOp",EDGE,"E10")])],"isStart":true});
            var Q3;
            Q3=makeQuery(id+"F1.opExtrude","CAP_EDGE",EDGE,{"disambiguationData":[OSD([sQuery(id+"F0.wireOp",EDGE,"E11")])],"isStart":false});
            var Q4;
            Q4=makeQuery(id+"F1.opExtrude","CAP_EDGE",EDGE,{"disambiguationData":[OSD([sQuery(id+"F0.wireOp",EDGE,"E9")])],"isStart":false});
            var Q5;
            Q5=makeQuery(id+"F1.opExtrude","CAP_EDGE",EDGE,{"disambiguationData":[OSD([sQuery(id+"F0.wireOp",EDGE,"E10")])],"isStart":false});
            fillet(context, id + "F6", {"entities" : qUnion([Q0, Q1, Q2, Q3, Q4, Q5]), "radius" : 2.5 * mm, "tangentPropagation" : true, "allowEdgeOverflow" : false});
        }
        {
            var Q0;
            {var subQ0=sQuery(id+"F0.wireOp",EDGE,"E25.trimOffspring");var subQ1=sQuery(id+"F0.wireOp",EDGE,"E24");var subQ2=makeQuery(id+"F0.imprint","INTERSECT",VERTEX,{"derivedFrom":[sQuery(id+"F0.wireOp",EDGE,"E10"),subQ1]});Q0=makeQuery(id+"F3.opChamfer","BLEND_EDGE",EDGE,{"blendedFrom":[makeQuery(id+"F1.opExtrude","CAP_EDGE",EDGE,{"disambiguationData":[OSD([subQ1]),TDD([makeQuery(id+"F0.imprint","IMPRINT",EDGE,{"disambiguationData":[TD([[makeQuery(id+"F0.imprint","INTERSECT",VERTEX,{"derivedFrom":[subQ1,subQ0]}),-1.0]])],"derivedFrom":subQ1}),makeQuery(id+"F0.imprint","IMPRINT",EDGE,{"disambiguationData":[TD([[subQ2,-1.0]])],"derivedFrom":subQ1})])],"isStart":false}),makeQuery(id+"F1.opExtrude","SWEPT_FACE",FACE,{"disambiguationData":[OSD([subQ0])]})],"blendedInto":[makeQuery(id+"F1.opExtrude","SWEPT_FACE",FACE,{"disambiguationData":[OSD([subQ0])]})]});}
            var Q1;
            {var subQ0=sQuery(id+"F0.wireOp",EDGE,"E25.trimOffspring");var subQ1=sQuery(id+"F0.wireOp",EDGE,"E24");var subQ2=makeQuery(id+"F0.imprint","INTERSECT",VERTEX,{"derivedFrom":[sQuery(id+"F0.wireOp",EDGE,"E10"),subQ1]});Q1=makeQuery(id+"F4.opChamfer","BLEND_EDGE",EDGE,{"blendedFrom":[makeQuery(id+"F1.opExtrude","CAP_EDGE",EDGE,{"disambiguationData":[OSD([subQ1]),TDD([makeQuery(id+"F0.imprint","IMPRINT",EDGE,{"disambiguationData":[TD([[makeQuery(id+"F0.imprint","INTERSECT",VERTEX,{"derivedFrom":[subQ1,subQ0]}),-1.0]])],"derivedFrom":subQ1}),makeQuery(id+"F0.imprint","IMPRINT",EDGE,{"disambiguationData":[TD([[subQ2,-1.0]])],"derivedFrom":subQ1})])],"isStart":true}),makeQuery(id+"F1.opExtrude","SWEPT_FACE",FACE,{"disambiguationData":[OSD([subQ0])]})],"blendedInto":[makeQuery(id+"F1.opExtrude","SWEPT_FACE",FACE,{"disambiguationData":[OSD([subQ0])]})]});}
            var Q2;
            {var subQ0=sQuery(id+"F0.wireOp",EDGE,"E26.trimOffspring");var subQ1=sQuery(id+"F0.wireOp",EDGE,"E23");var subQ2=makeQuery(id+"F0.imprint","INTERSECT",VERTEX,{"derivedFrom":[sQuery(id+"F0.wireOp",EDGE,"E9"),subQ1]});Q2=makeQuery(id+"F3.opChamfer","BLEND_EDGE",EDGE,{"blendedFrom":[makeQuery(id+"F1.opExtrude","CAP_EDGE",EDGE,{"disambiguationData":[OSD([subQ1]),TDD([makeQuery(id+"F0.imprint","IMPRINT",EDGE,{"disambiguationData":[TD([[makeQuery(id+"F0.imprint","INTERSECT",VERTEX,{"derivedFrom":[subQ1,subQ0]}),-1.0]])],"derivedFrom":subQ1}),makeQuery(id+"F0.imprint","IMPRINT",EDGE,{"disambiguationData":[TD([[subQ2,-1.0]])],"derivedFrom":subQ1})])],"isStart":false}),makeQuery(id+"F1.opExtrude","SWEPT_FACE",FACE,{"disambiguationData":[OSD([subQ0])]})],"blendedInto":[makeQuery(id+"F1.opExtrude","SWEPT_FACE",FACE,{"disambiguationData":[OSD([subQ0])]})]});}
            var Q3;
            {var subQ0=sQuery(id+"F0.wireOp",EDGE,"E26.trimOffspring");var subQ1=sQuery(id+"F0.wireOp",EDGE,"E23");var subQ2=makeQuery(id+"F0.imprint","INTERSECT",VERTEX,{"derivedFrom":[sQuery(id+"F0.wireOp",EDGE,"E9"),subQ1]});Q3=makeQuery(id+"F4.opChamfer","BLEND_EDGE",EDGE,{"blendedFrom":[makeQuery(id+"F1.opExtrude","CAP_EDGE",EDGE,{"disambiguationData":[OSD([subQ1]),TDD([makeQuery(id+"F0.imprint","IMPRINT",EDGE,{"disambiguationData":[TD([[makeQuery(id+"F0.imprint","INTERSECT",VERTEX,{"derivedFrom":[subQ1,subQ0]}),-1.0]])],"derivedFrom":subQ1}),makeQuery(id+"F0.imprint","IMPRINT",EDGE,{"disambiguationData":[TD([[subQ2,-1.0]])],"derivedFrom":subQ1})])],"isStart":true}),makeQuery(id+"F1.opExtrude","SWEPT_FACE",FACE,{"disambiguationData":[OSD([subQ0])]})],"blendedInto":[makeQuery(id+"F1.opExtrude","SWEPT_FACE",FACE,{"disambiguationData":[OSD([subQ0])]})]});}
            var Q4;
            {var subQ0=sQuery(id+"F0.wireOp",EDGE,"E1");var subQ1=sQuery(id+"F0.wireOp",EDGE,"E22");var subQ2=makeQuery(id+"F0.imprint","INTERSECT",VERTEX,{"derivedFrom":[sQuery(id+"F0.wireOp",EDGE,"E11"),subQ1]});Q4=makeQuery(id+"F4.opChamfer","BLEND_EDGE",EDGE,{"blendedFrom":[makeQuery(id+"F1.opExtrude","CAP_EDGE",EDGE,{"disambiguationData":[OSD([subQ1]),TDD([makeQuery(id+"F0.imprint","IMPRINT",EDGE,{"disambiguationData":[TD([[makeQuery(id+"F0.imprint","INTERSECT",VERTEX,{"derivedFrom":[subQ0,subQ1]}),-1.0]])],"derivedFrom":subQ1}),makeQuery(id+"F0.imprint","IMPRINT",EDGE,{"disambiguationData":[TD([[subQ2,-1.0]])],"derivedFrom":subQ1})])],"isStart":true}),makeQuery(id+"F1.opExtrude","SWEPT_FACE",FACE,{"disambiguationData":[OSD([subQ0])]})],"blendedInto":[makeQuery(id+"F1.opExtrude","SWEPT_FACE",FACE,{"disambiguationData":[OSD([subQ0])]})]});}
            var Q5;
            {var subQ0=sQuery(id+"F0.wireOp",EDGE,"E1");var subQ1=sQuery(id+"F0.wireOp",EDGE,"E22");var subQ2=makeQuery(id+"F0.imprint","INTERSECT",VERTEX,{"derivedFrom":[sQuery(id+"F0.wireOp",EDGE,"E11"),subQ1]});Q5=makeQuery(id+"F3.opChamfer","BLEND_EDGE",EDGE,{"blendedFrom":[makeQuery(id+"F1.opExtrude","CAP_EDGE",EDGE,{"disambiguationData":[OSD([subQ1]),TDD([makeQuery(id+"F0.imprint","IMPRINT",EDGE,{"disambiguationData":[TD([[makeQuery(id+"F0.imprint","INTERSECT",VERTEX,{"derivedFrom":[subQ0,subQ1]}),-1.0]])],"derivedFrom":subQ1}),makeQuery(id+"F0.imprint","IMPRINT",EDGE,{"disambiguationData":[TD([[subQ2,-1.0]])],"derivedFrom":subQ1})])],"isStart":false}),makeQuery(id+"F1.opExtrude","SWEPT_FACE",FACE,{"disambiguationData":[OSD([subQ0])]})],"blendedInto":[makeQuery(id+"F1.opExtrude","SWEPT_FACE",FACE,{"disambiguationData":[OSD([subQ0])]})]});}
            fillet(context, id + "F7", {"entities" : qUnion([Q0, Q1, Q2, Q3, Q4, Q5]), "radius" : 1 * mm, "allowEdgeOverflow" : false});
        }
    });
